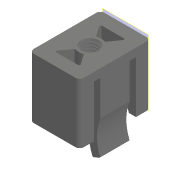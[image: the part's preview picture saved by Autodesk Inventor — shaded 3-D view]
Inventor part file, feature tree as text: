
AUTODESK INVENTOR PART (.ipt)
format: ipt  version: 2021 (Build 250183000, 183)  size: 411,648 bytes
history: native  units: mm
features: plane x1, split x1, other x1
ambient origin geometry x8: Origin, YZ Plane, XZ Plane, XY Plane, X Axis, Y Axis, Z Axis, Center Point
bodies: Solid1 (feature_tree)
feature tree (3):
  plane  "Work Plane2"
  split  "Split1"
  other  "Austragung1"
